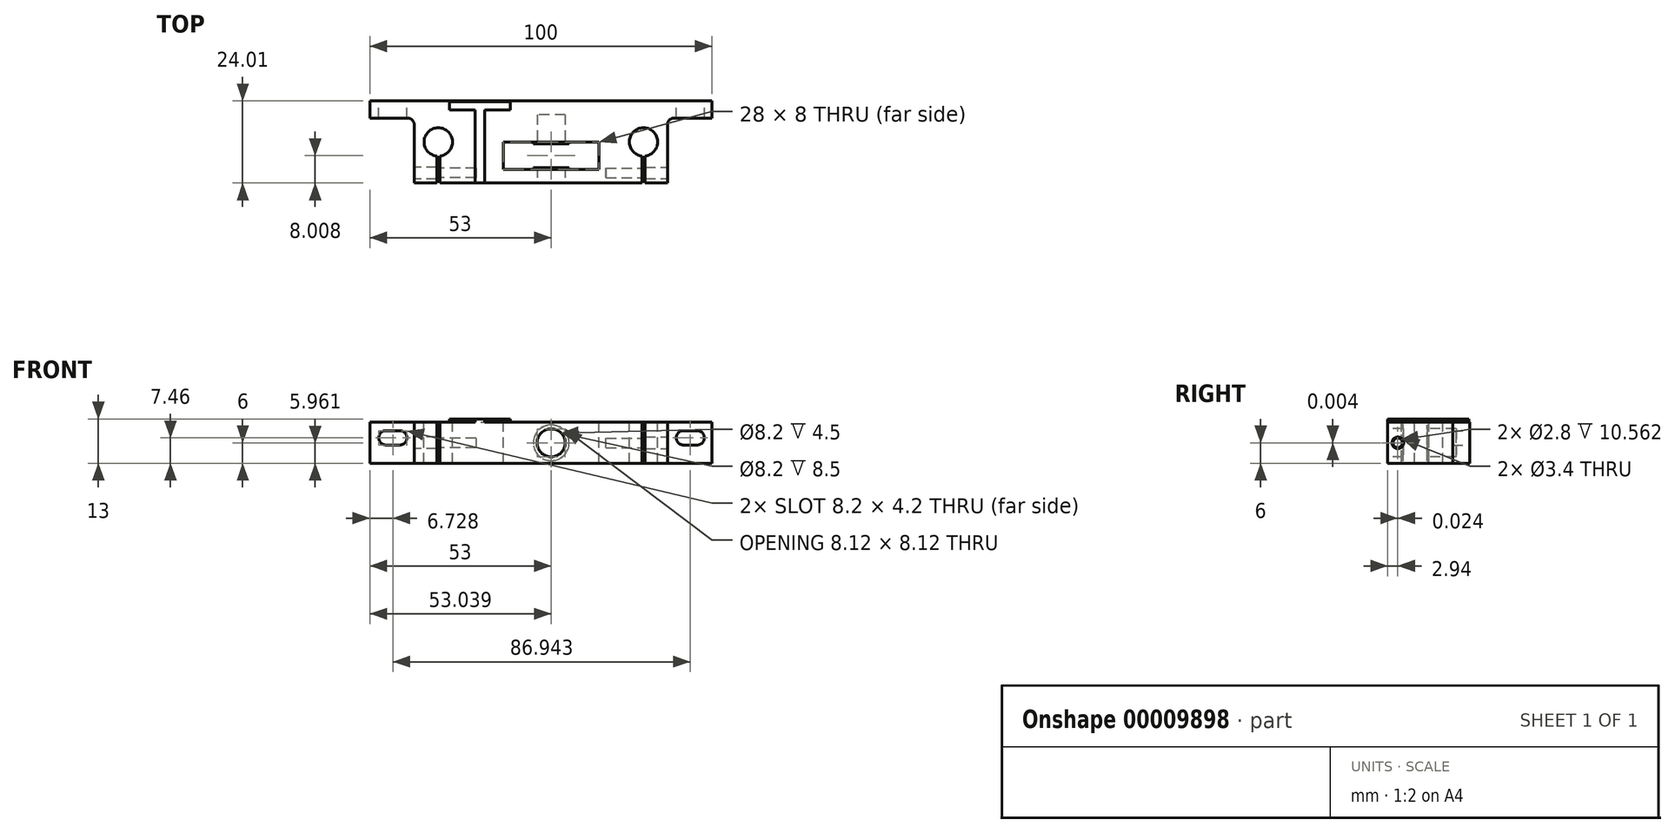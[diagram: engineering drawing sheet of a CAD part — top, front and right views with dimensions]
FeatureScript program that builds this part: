
annotation { "Feature Type Name" : "Feature", "Feature Type Description" : "" }
export const myFeature = defineFeature(function(context is Context, id is Id, definition is map)
    precondition{}
    {
        {
            var Q0;
            Q0=qCreatedBy(makeId("Top.planeOp"),FACE);
            var sketch = newSketch(context, id + "F0", { "sketchPlane" : qUnion([Q0])});
            skLineSegment(sketch, "E0", {"start": v(-46.35, 12.3) * mm, "end": v(53.65, 12.3) * mm});
            skLineSegment(sketch, "E1", {"start": v(53.65, 12.3) * mm, "end": v(53.65, 7.3) * mm});
            skLineSegment(sketch, "E2", {"start": v(53.65, 7.3) * mm, "end": v(40.65, 7.3) * mm});
            skLineSegment(sketch, "E3", {"start": v(40.65, 7.3) * mm, "end": v(40.65, -11.7) * mm});
            skLineSegment(sketch, "E4", {"start": v(40.65, -11.7) * mm, "end": v(-33.35, -11.7) * mm});
            skLineSegment(sketch, "E5", {"start": v(-33.35, -11.7) * mm, "end": v(-33.35, 7.3) * mm});
            skLineSegment(sketch, "E6", {"start": v(-33.35, 7.3) * mm, "end": v(-46.35, 7.3) * mm});
            skLineSegment(sketch, "E7", {"start": v(-46.35, 7.3) * mm, "end": v(-46.35, 12.3) * mm});
            skSolve(sketch);
        }
        {
            var Q0;
            Q0 = qSketchRegion(id + "F0", true);
            extrude(context, id + "F1", {"entities" : qUnion([Q0]), "depth" : 12 * mm});
        }
        {
            var Q0;
            Q0=makeQuery(id+"F1.opExtrude","CAP_FACE",FACE,{"disambiguationData":[OSD([sQuery(id+"F0.wireOp",EDGE,"E0"),sQuery(id+"F0.wireOp",EDGE,"E1"),sQuery(id+"F0.wireOp",EDGE,"E2"),sQuery(id+"F0.wireOp",EDGE,"E3"),sQuery(id+"F0.wireOp",EDGE,"E4"),sQuery(id+"F0.wireOp",EDGE,"E5"),sQuery(id+"F0.wireOp",EDGE,"E6"),sQuery(id+"F0.wireOp",EDGE,"E7")])],"isStart":false});
            var sketch = newSketch(context, id + "F2", { "sketchPlane" : qUnion([Q0])});
            skCircle(sketch, "E8", {"center": v(-26.35, 0.3) * mm, "radius": 4.15 * mm});
            skCircle(sketch, "E9", {"center": v(33.65, 0.3) * mm, "radius": 4.15 * mm});
            skPoint(sketch, "E10", {"position": v(3.65, 12.3) * mm});
            skLineSegment(sketch, "E11.bottom", {"start": v(33.21, -3.01) * mm, "end": v(34.09, -3.01) * mm});
            skLineSegment(sketch, "E11.top", {"start": v(33.21, -12.27) * mm, "end": v(34.09, -12.27) * mm});
            skLineSegment(sketch, "E11.left", {"start": v(33.21, -3.01) * mm, "end": v(33.21, -12.27) * mm});
            skLineSegment(sketch, "E11.right", {"start": v(34.09, -3.01) * mm, "end": v(34.09, -12.27) * mm});
            skPoint(sketch, "E12", {"position": v(33.65, -3.01) * mm});
            skLineSegment(sketch, "E13", {"start": v(3.65, 12.3) * mm, "end": v(3.65, -11.7) * mm, "construction": true});
            skLineSegment(sketch, "E14.MirrorCS", {"start": v(-25.91, -12.27) * mm, "end": v(-26.79, -12.27) * mm});
            skLineSegment(sketch, "E15.MirrorCS", {"start": v(-26.79, -3.01) * mm, "end": v(-26.79, -12.27) * mm});
            skLineSegment(sketch, "E16.MirrorCS", {"start": v(-25.91, -3.01) * mm, "end": v(-26.79, -3.01) * mm});
            skLineSegment(sketch, "E17.MirrorCS", {"start": v(-25.91, -3.01) * mm, "end": v(-25.91, -12.27) * mm});
            skSolve(sketch);
        }
        {
            var Q0;
            Q0 = qSketchRegion(id + "F2", true);
            var Q1;
            {var subQ3=sQuery(id+"F2.wireOp",EDGE,"E11.bottom");Q1=makeQuery(id+"F2.imprint","IMPRINT",FACE,{"disambiguationData":[TD([[makeQuery(id+"F2.imprint","IMPRINT",EDGE,{"derivedFrom":subQ3}),-1.0]])]});}
            var Q2;
            {var subQ3=sQuery(id+"F2.wireOp",EDGE,"E16.MirrorCS");Q2=makeQuery(id+"F2.imprint","IMPRINT",FACE,{"disambiguationData":[TD([[makeQuery(id+"F2.imprint","IMPRINT",EDGE,{"derivedFrom":subQ3}),1.0]])]});}
            extrude(context, id + "F3", {"entities" : qUnion([Q0, Q1, Q2]), "operationType" : NewBodyOperationType.REMOVE, "endBound" : BoundingType.THROUGH_ALL, "oppositeDirection" : true, "depth" : 25 * mm});
        }
        {
            var Q0;
            Q0=makeQuery(id+"F1.opExtrude","SWEPT_FACE",FACE,{"disambiguationData":[OSD([sQuery(id+"F0.wireOp",EDGE,"E0")])]});
            var sketch = newSketch(context, id + "F4", { "sketchPlane" : qUnion([Q0])});
            skLineSegment(sketch, "E18", {"start": v(-53.65, 7.46) * mm, "end": v(46.35, 7.46) * mm, "construction": true});
            skLineSegment(sketch, "E19.bottom", {"start": v(-49.32, 9.56) * mm, "end": v(-45.32, 9.56) * mm});
            skLineSegment(sketch, "E19.top", {"start": v(-49.32, 5.36) * mm, "end": v(-45.32, 5.36) * mm});
            skArc(sketch, "E20", {"start": v(-45.32, 5.36) * mm, "mid": v(-43.22, 7.46) * mm, "end": v(-45.32, 9.56) * mm});
            skArc(sketch, "E21", {"start": v(-49.32, 9.56) * mm, "mid": v(-51.42, 7.46) * mm, "end": v(-49.32, 5.36) * mm});
            skLineSegment(sketch, "E22.top", {"start": v(37.62, 5.36) * mm, "end": v(41.62, 5.36) * mm});
            skLineSegment(sketch, "E22.bottom", {"start": v(37.62, 9.56) * mm, "end": v(41.62, 9.56) * mm});
            skArc(sketch, "E23", {"start": v(37.62, 9.56) * mm, "mid": v(35.52, 7.46) * mm, "end": v(37.62, 5.36) * mm});
            skArc(sketch, "E24", {"start": v(41.62, 5.36) * mm, "mid": v(43.72, 7.46) * mm, "end": v(41.62, 9.56) * mm});
            skSolve(sketch);
        }
        {
            var Q0;
            Q0 = qSketchRegion(id + "F4", true);
            extrude(context, id + "F5", {"entities" : qUnion([Q0]), "operationType" : NewBodyOperationType.REMOVE, "endBound" : BoundingType.THROUGH_ALL, "oppositeDirection" : true, "depth" : 25 * mm});
        }
        {
            var Q0;
            Q0=makeQuery(id+"F1.opExtrude","SWEPT_FACE",FACE,{"disambiguationData":[OSD([sQuery(id+"F0.wireOp",EDGE,"E4")])]});
            var sketch = newSketch(context, id + "F6", { "sketchPlane" : qUnion([Q0])});
            skLineSegment(sketch, "E25", {"start": v(-33.35, 6) * mm, "end": v(40.65, 6) * mm, "construction": true});
            skCircle(sketch, "E26", {"center": v(6.65, 6) * mm, "radius": 4.1 * mm});
            skSolve(sketch);
        }
        {
            var Q0;
            Q0 = qSketchRegion(id + "F6", true);
            extrude(context, id + "F7", {"entities" : qUnion([Q0]), "operationType" : NewBodyOperationType.REMOVE, "oppositeDirection" : true, "depth" : 20 * mm});
        }
        {
            var Q0;
            Q0=makeQuery(id+"F1.opExtrude","CAP_FACE",FACE,{"disambiguationData":[OSD([sQuery(id+"F0.wireOp",EDGE,"E0"),sQuery(id+"F0.wireOp",EDGE,"E1"),sQuery(id+"F0.wireOp",EDGE,"E2"),sQuery(id+"F0.wireOp",EDGE,"E3"),sQuery(id+"F0.wireOp",EDGE,"E4"),sQuery(id+"F0.wireOp",EDGE,"E5"),sQuery(id+"F0.wireOp",EDGE,"E6"),sQuery(id+"F0.wireOp",EDGE,"E7")])],"isStart":false});
            var sketch = newSketch(context, id + "F8", { "sketchPlane" : qUnion([Q0])});
            skLineSegment(sketch, "E27.bottom", {"start": v(-7.35, 0.3) * mm, "end": v(20.65, 0.3) * mm});
            skLineSegment(sketch, "E27.top", {"start": v(-7.35, -7.7) * mm, "end": v(20.65, -7.7) * mm});
            skLineSegment(sketch, "E27.left", {"start": v(-7.35, 0.3) * mm, "end": v(-7.35, -7.7) * mm});
            skLineSegment(sketch, "E27.right", {"start": v(20.65, 0.3) * mm, "end": v(20.65, -7.7) * mm});
            skLineSegment(sketch, "E28", {"start": v(6.65, 12.3) * mm, "end": v(6.65, -11.7) * mm, "construction": true});
            skLineSegment(sketch, "E29", {"start": v(6.65, 0.3) * mm, "end": v(6.65, -7.7) * mm});
            skSolve(sketch);
        }
        {
            var Q0;
            Q0 = qSketchRegion(id + "F8", true);
            extrude(context, id + "F9", {"entities" : qUnion([Q0]), "operationType" : NewBodyOperationType.REMOVE, "endBound" : BoundingType.THROUGH_ALL, "oppositeDirection" : true, "depth" : 25 * mm});
        }
        {
            var Q0;
            Q0=makeQuery(id+"F9.boolean.opBoolean","COPY",FACE,{"derivedFrom":makeQuery(id+"F9.opExtrude","SWEPT_FACE",FACE,{"disambiguationData":[OSD([sQuery(id+"F8.wireOp",EDGE,"E27.bottom")])]})});
            var sketch = newSketch(context, id + "F10", { "sketchPlane" : qUnion([Q0])});
            skCircle(sketch, "E30", {"center": v(6.65, 6) * mm, "radius": 5.2 * mm});
            skSolve(sketch);
        }
        {
            var Q0;
            Q0=makeQuery(id+"F10.imprint","IMPRINT",FACE,{"disambiguationData":[TD([[makeQuery(id+"F10.imprint","IMPRINT",EDGE,{"derivedFrom":sQuery(id+"F10.wireOp",EDGE,"E30")}),1.0]])]});
            extrude(context, id + "F11", {"entities" : qUnion([Q0]), "operationType" : NewBodyOperationType.ADD, "depth" : 0.5 * mm});
        }
        {
            var Q0;
            Q0=makeQuery(id+"F9.boolean.opBoolean","COPY",FACE,{"derivedFrom":makeQuery(id+"F9.opExtrude","SWEPT_FACE",FACE,{"disambiguationData":[OSD([sQuery(id+"F8.wireOp",EDGE,"E27.top")])]})});
            var sketch = newSketch(context, id + "F12", { "sketchPlane" : qUnion([Q0])});
            skCircle(sketch, "E31", {"center": v(-6.65, 6) * mm, "radius": 5.25 * mm});
            skSolve(sketch);
        }
        {
            var Q0;
            Q0=makeQuery(id+"F12.imprint","IMPRINT",FACE,{"disambiguationData":[TD([[makeQuery(id+"F12.imprint","IMPRINT",EDGE,{"derivedFrom":sQuery(id+"F12.wireOp",EDGE,"E31")}),1.0]])]});
            extrude(context, id + "F13", {"entities" : qUnion([Q0]), "operationType" : NewBodyOperationType.ADD, "depth" : 0.5 * mm});
        }
        {
            var Q0;
            Q0=makeQuery(id+"F1.opExtrude","CAP_FACE",FACE,{"disambiguationData":[OSD([sQuery(id+"F0.wireOp",EDGE,"E0"),sQuery(id+"F0.wireOp",EDGE,"E1"),sQuery(id+"F0.wireOp",EDGE,"E2"),sQuery(id+"F0.wireOp",EDGE,"E3"),sQuery(id+"F0.wireOp",EDGE,"E4"),sQuery(id+"F0.wireOp",EDGE,"E5"),sQuery(id+"F0.wireOp",EDGE,"E6"),sQuery(id+"F0.wireOp",EDGE,"E7")])],"isStart":false});
            var sketch = newSketch(context, id + "F14", { "sketchPlane" : qUnion([Q0])});
            skText(sketch, "E32", { "text": "T", "fontName": "OpenSans-Regular.ttf"});
            const initialGuessF14  = {"E32": [-0.02337, -0.0117, 1, 0, 0.024]};
            skSetInitialGuess(sketch, initialGuessF14);
            skSolve(sketch);
        }
        {
            var Q0;
            Q0 = qSketchRegion(id + "F14", true);
            extrude(context, id + "F15", {"entities" : qUnion([Q0]), "operationType" : NewBodyOperationType.ADD, "depth" : 1 * mm});
        }
        {
            var Q0;
            Q0=makeQuery(id+"F1.opExtrude","SWEPT_FACE",FACE,{"disambiguationData":[OSD([sQuery(id+"F0.wireOp",EDGE,"E3")])]});
            var sketch = newSketch(context, id + "F16", { "sketchPlane" : qUnion([Q0])});
            skCircle(sketch, "E33", {"center": v(-8.74, 6) * mm, "radius": 1.7 * mm});
            skCircle(sketch, "E34", {"center": v(-8.74, 6) * mm, "radius": 1.4 * mm});
            skLineSegment(sketch, "E35", {"start": v(-11.7, 6) * mm, "end": v(-3.84, 6) * mm, "construction": true});
            skSolve(sketch);
        }
        {
            var Q0;
            Q0=makeQuery(id+"F16.imprint","IMPRINT",FACE,{"disambiguationData":[TD([[makeQuery(id+"F16.imprint","IMPRINT",EDGE,{"derivedFrom":sQuery(id+"F16.wireOp",EDGE,"E34")}),1.0]])]});
            extrude(context, id + "F17", {"entities" : qUnion([Q0]), "operationType" : NewBodyOperationType.REMOVE, "oppositeDirection" : true, "depth" : 18 * mm});
        }
        {
            var Q0;
            Q0=makeQuery(id+"F16.imprint","IMPRINT",FACE,{"disambiguationData":[TD([[makeQuery(id+"F16.imprint","IMPRINT",EDGE,{"derivedFrom":sQuery(id+"F16.wireOp",EDGE,"E34")}),1.0]])]});
            var Q1;
            Q1=makeQuery(id+"F16.imprint","IMPRINT",FACE,{"disambiguationData":[TD([[makeQuery(id+"F16.imprint","IMPRINT",EDGE,{"derivedFrom":sQuery(id+"F16.wireOp",EDGE,"E33")}),1.0]])]});
            extrude(context, id + "F18", {"entities" : qUnion([Q0, Q1]), "operationType" : NewBodyOperationType.REMOVE, "endBound" : BoundingType.UP_TO_NEXT, "oppositeDirection" : true, "depth" : 7 * mm});
        }
        {
            var Q0;
            Q0=makeQuery(id+"F1.opExtrude","SWEPT_EDGE",EDGE,{"disambiguationData":[OSD([sQuery(id+"F0.wireOp",EDGE,"E2"),sQuery(id+"F0.wireOp",EDGE,"E3")])]});
            fillet(context, id + "F19", {"entities" : qUnion([Q0]), "radius" : 2 * mm, "tangentPropagation" : true, "allowEdgeOverflow" : false});
        }
        {
            var Q0;
            Q0=makeQuery(id+"F1.opExtrude","SWEPT_FACE",FACE,{"disambiguationData":[OSD([sQuery(id+"F0.wireOp",EDGE,"E5")])]});
            var sketch = newSketch(context, id + "F20", { "sketchPlane" : qUnion([Q0])});
            skCircle(sketch, "E36", {"center": v(8.76, 6) * mm, "radius": 1.7 * mm});
            skCircle(sketch, "E37", {"center": v(8.76, 6) * mm, "radius": 1.4 * mm});
            skLineSegment(sketch, "E38", {"start": v(8.76, 0) * mm, "end": v(8.76, 12) * mm, "construction": true});
            skSolve(sketch);
        }
        {
            var Q0;
            Q0=makeQuery(id+"F20.imprint","IMPRINT",FACE,{"disambiguationData":[TD([[makeQuery(id+"F20.imprint","IMPRINT",EDGE,{"derivedFrom":sQuery(id+"F20.wireOp",EDGE,"E37")}),1.0]])]});
            extrude(context, id + "F21", {"entities" : qUnion([Q0]), "operationType" : NewBodyOperationType.REMOVE, "oppositeDirection" : true, "depth" : 18 * mm});
        }
        {
            var Q0;
            Q0=makeQuery(id+"F20.imprint","IMPRINT",FACE,{"disambiguationData":[TD([[makeQuery(id+"F20.imprint","IMPRINT",EDGE,{"derivedFrom":sQuery(id+"F20.wireOp",EDGE,"E37")}),1.0]])]});
            var Q1;
            Q1=makeQuery(id+"F20.imprint","IMPRINT",FACE,{"disambiguationData":[TD([[makeQuery(id+"F20.imprint","IMPRINT",EDGE,{"derivedFrom":sQuery(id+"F20.wireOp",EDGE,"E36")}),1.0]])]});
            extrude(context, id + "F22", {"entities" : qUnion([Q0, Q1]), "operationType" : NewBodyOperationType.REMOVE, "endBound" : BoundingType.UP_TO_NEXT, "oppositeDirection" : true, "depth" : 25 * mm});
        }
        {
            var Q0;
            Q0=makeQuery(id+"F1.opExtrude","SWEPT_EDGE",EDGE,{"disambiguationData":[OSD([sQuery(id+"F0.wireOp",EDGE,"E5"),sQuery(id+"F0.wireOp",EDGE,"E6")])]});
            fillet(context, id + "F23", {"entities" : qUnion([Q0]), "radius" : 2 * mm, "tangentPropagation" : true, "allowEdgeOverflow" : false});
        }
    });
